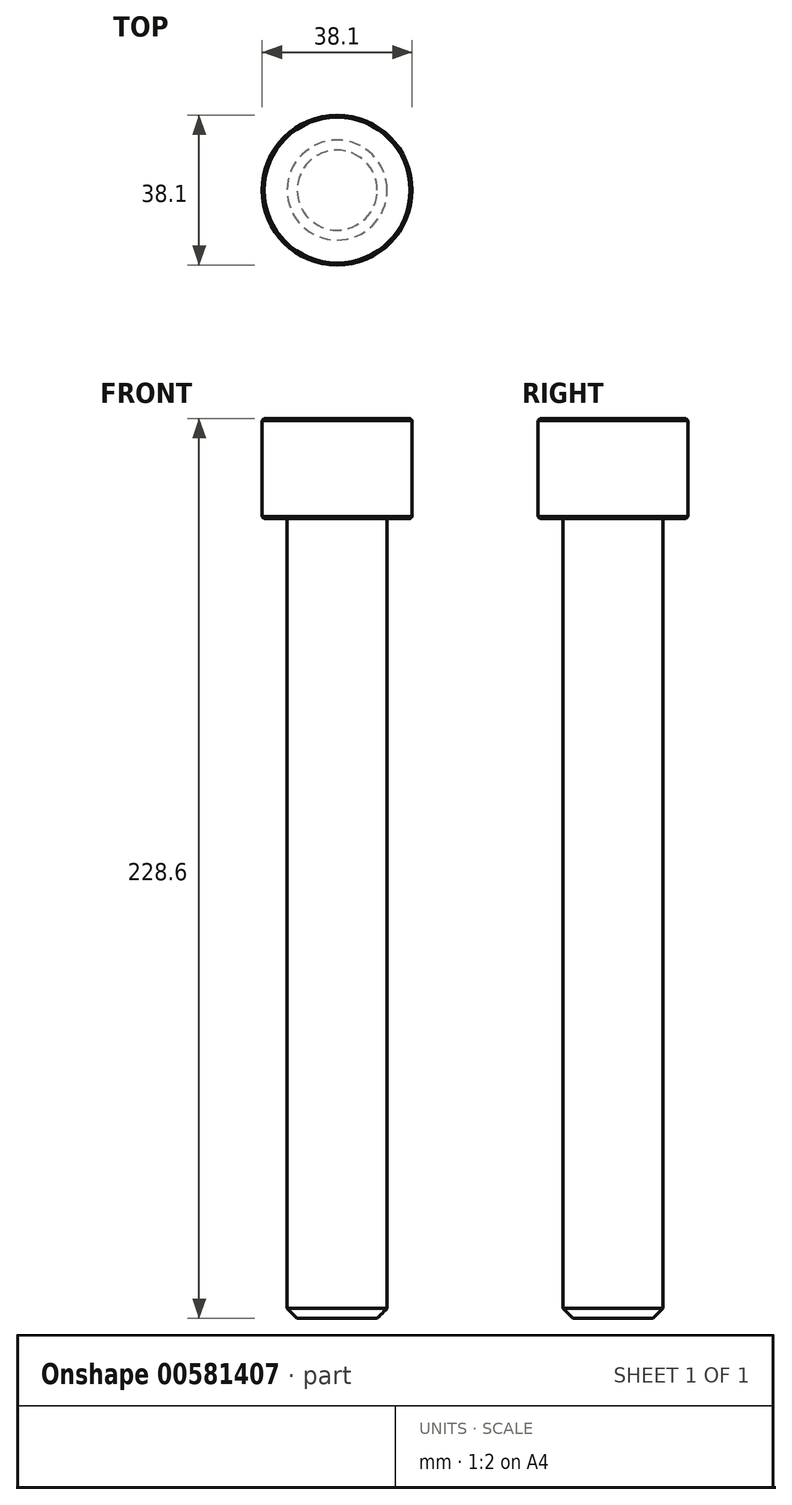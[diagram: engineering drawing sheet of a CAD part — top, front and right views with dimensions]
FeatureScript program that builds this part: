
annotation { "Feature Type Name" : "Feature", "Feature Type Description" : "" }
export const myFeature = defineFeature(function(context is Context, id is Id, definition is map)
    precondition{}
    {
        {
            var Q0;
            Q0=qCreatedBy(makeId("Top.planeOp"),FACE);
            var sketch = newSketch(context, id + "F0", { "sketchPlane" : qUnion([Q0])});
            skCircle(sketch, "E0", {"center": v(0, 0) * mm, "radius": 12.7 * mm});
            skSolve(sketch);
        }
        {
            var Q0;
            Q0=makeQuery(id+"F0.imprint","IMPRINT",FACE,{"disambiguationData":[TD([[makeQuery(id+"F0.imprint","IMPRINT",EDGE,{"derivedFrom":sQuery(id+"F0.wireOp",EDGE,"E0")}),1.0]])]});
            extrude(context, id + "F1", {"entities" : qUnion([Q0]), "endBound" : BoundingType.SYMMETRIC, "depth" : 203.2 * mm, "offsetDistance" : 25.4 * mm});
        }
        {
            var Q0;
            Q0=makeQuery(id+"F1.opExtrude","CAP_EDGE",EDGE,{"disambiguationData":[OSD([sQuery(id+"F0.wireOp",EDGE,"E0")])],"isStart":true});
            chamfer(context, id + "F2", {"entities" : qUnion([Q0]), "width" : 2.54 * mm, "tangentPropagation" : true});
        }
        {
            var Q0;
            Q0=makeQuery(id+"F1.opExtrude","CAP_FACE",FACE,{"disambiguationData":[OSD([sQuery(id+"F0.wireOp",EDGE,"E0")])],"isStart":false});
            var sketch = newSketch(context, id + "F3", { "sketchPlane" : qUnion([Q0])});
            skCircle(sketch, "E1", {"center": v(0, 0) * mm, "radius": 19.05 * mm});
            skSolve(sketch);
        }
        {
            var Q0;
            Q0=makeQuery(id+"F3.imprint","IMPRINT",FACE,{"disambiguationData":[TD([[makeQuery(id+"F3.imprint","IMPRINT",EDGE,{"derivedFrom":sQuery(id+"F3.wireOp",EDGE,"E1")}),1.0]])]});
            var Q1;
            Q1=makeQuery(id+"F3.imprint","IMPRINT",FACE,{"disambiguationData":[TD([[makeQuery(id+"F3.imprint","IMPRINT",EDGE,{"derivedFrom":makeQuery(id+"F1.opExtrude","CAP_EDGE",EDGE,{"disambiguationData":[OSD([sQuery(id+"F0.wireOp",EDGE,"E0")])],"isStart":false})}),1.0]])]});
            extrude(context, id + "F4", {"entities" : qUnion([Q0, Q1]), "operationType" : NewBodyOperationType.ADD, "depth" : 25.4 * mm, "offsetDistance" : 25.4 * mm});
        }
        {
            var Q0;
            Q0=makeQuery(id+"F4.opExtrude","CAP_EDGE",EDGE,{"disambiguationData":[OSD([sQuery(id+"F3.wireOp",EDGE,"E1")])],"isStart":false});
            var Q1;
            Q1=makeQuery(id+"F4.opExtrude","CAP_EDGE",EDGE,{"disambiguationData":[OSD([sQuery(id+"F3.wireOp",EDGE,"E1")])],"isStart":true});
            chamfer(context, id + "F5", {"entities" : qUnion([Q0, Q1]), "width" : 0.5 * mm, "tangentPropagation" : true});
        }
    });
